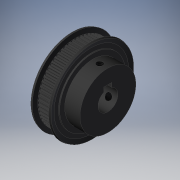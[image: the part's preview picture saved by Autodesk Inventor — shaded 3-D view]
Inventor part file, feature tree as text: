
AUTODESK INVENTOR PART (.ipt)
format: ipt  version: 2019 (Build 230136000, 136)  size: 564,224 bytes
history: native  units: mm
features: other x14, sketch x7, revolve x5, extrude x2, thread x2, pattern_circular x1
ambient origin geometry x8: Origin, YZ Plane, XZ Plane, XY Plane, X Axis, Y Axis, Z Axis, Center Point
bodies: Solid1 (feature_tree)
feature tree (31):
  revolve  "Revolution1"  [1 undecoded]
  extrude  "Extrusion1"  TaperAngle=360.0deg  [1 undecoded]
  pattern_circular  "Circular Pattern1"  [2 undecoded]
  revolve  "Revolution2"  [1 undecoded]
  revolve  "Revolution3"  [1 undecoded]
  revolve  "Revolution4"  [1 undecoded]
  thread  "Thread1"  [1 undecoded]
  revolve  "Revolution5"  [1 undecoded]
  thread  "Thread2"  [1 undecoded]
  extrude  "Extrusion2"  [1 undecoded]
  other  "to_screw_B1_XY"
  other  "to_screw_B1_YZ"
  other  "to_screw_B1_ZX"
  other  "to_screw_B1_X"
  other  "to_screw_B1_Y"
  other  "to_screw_B1_Z"
  other  "to_screw_B1_Center"
  other  "to_screw_B2_XY"
  other  "to_screw_B2_YZ"
  other  "to_screw_B2_ZX"
  other  "to_screw_B2_X"
  other  "to_screw_B2_Y"
  other  "to_screw_B2_Z"
  other  "to_screw_B2_Center"
  sketch  "Sketch_17"  dims[d8=360.0deg]
  sketch  "Sketch_18"  dims[d9=7.2mm d10=0.0mm]
  sketch  "Sketch_20"  dims[d11=360.0deg]
  sketch  "Sketch_21"  dims[d12=9.0mm d13=0.0mm d14=18.0mm d15=0.0mm d16=0.0mm]
  sketch  "Sketch_1"  dims[d0=360.0deg d1=7.0mm d2=0.0mm]
  sketch  "Sketch_2"  dims[d3=600.0mm d4=1.047198mm d6=360.0deg]
  sketch  "Sketch_3"  dims[d7=360.0deg]
note: 11 required parameter values undecoded (feature->parameter linkage not recoverable at this tier; creation-order binding heuristic only, values carry confidence <= 0.55)